# Revit family: Haworth_Janus_Quinta_Chair_Side
name_source: partatom
category: Furniture
revit_build: Autodesk Revit 2018 (Build: 20170223_1515(x64)
units: mm (PartAtom-declared; Revit-internal decimal feet)

## family parameters
Always vertical = Yes
Cut with Voids When Loaded = No
OmniClass Number = 23.40.70.14.64.21
OmniClass Title = Systems Furniture
Room Calculation Point = No
Shared = No
Work Plane-Based = No

## types (8) — shared parameters
Actual Depth = 25 3/4"
Actual Height = 36"
Assembly Code = E2020200
Glide Finish = Haworth _ Polymer _ Black
Manufacturer = Haworth
Revision Number = 2
Seat Height = 18 1/4"
Size = Verify Final Dim. w/ Haworth
URL = http://www.haworth.com
URL - Product = https://www.haworth.com
Warranty = https://www.haworth.com

## per-type parameters (varying)
| type | Actual Width | Arm Height | Cushion | Description | Model | With Arms | Without Arms |
| HCJC-QN-SA-J - With Arms - Fiber Frame - With Cushion | 23 1/2" | 26 1/4" | Yes | Haworth Janus Quinta - Side Chair with Arms | HCJC-QN-SA-J | Yes | No |
| HCJC-QN-SN-W - Without Arms - Wood Frame - With Cushion | 20 1/2" | 18 1/4" | Yes | Haworth Janus Quinta - Side Chair | HCJC-QN-SN-W | No | Yes |
| HCJC-QN-SA-J - With Arms - Fiber Frame - No Cushion | 23 1/2" | 26 1/4" | No | Haworth Janus Quinta - Side Chair with Arms | HCJC-QN-SA-J | Yes | No |
| HCJC-QN-SN-J - Without Arms - Fiber Frame - No Cushion | 20 1/2" | 18 1/4" | No | Haworth Janus Quinta - Side Chair | HCJC-QN-SN-J | No | Yes |
| HCJC-QN-SA-W - With Arms - Wood Frame - No Cushion | 23 1/2" | 26 1/4" | No | Haworth Janus Quinta - Side Chair with Arms | HCJC-QN-SA-W | Yes | No |
| HCJC-QN-SA-W - With Arms - Wood Frame - With Cushion | 23 1/2" | 26 1/4" | Yes | Haworth Janus Quinta - Side Chair with Arms | HCJC-QN-SA-W | Yes | No |
| HCJC-QN-SN-W - Without Arms - Wood Frame - No Cushion | 20 1/2" | 18 1/4" | No | Haworth Janus Quinta - Side Chair | HCJC-QN-SN-W | No | Yes |
| HCJC-QN-SN-J - Without Arms - Fiber Frame - With Cushion | 20 1/2" | 18 1/4" | Yes | Haworth Janus Quinta - Side Chair | HCJC-QN-SN-J | No | Yes |

## geometry (parser evidence)
native form markers: Sweep x8
no freeform markers — native parametric forms only
